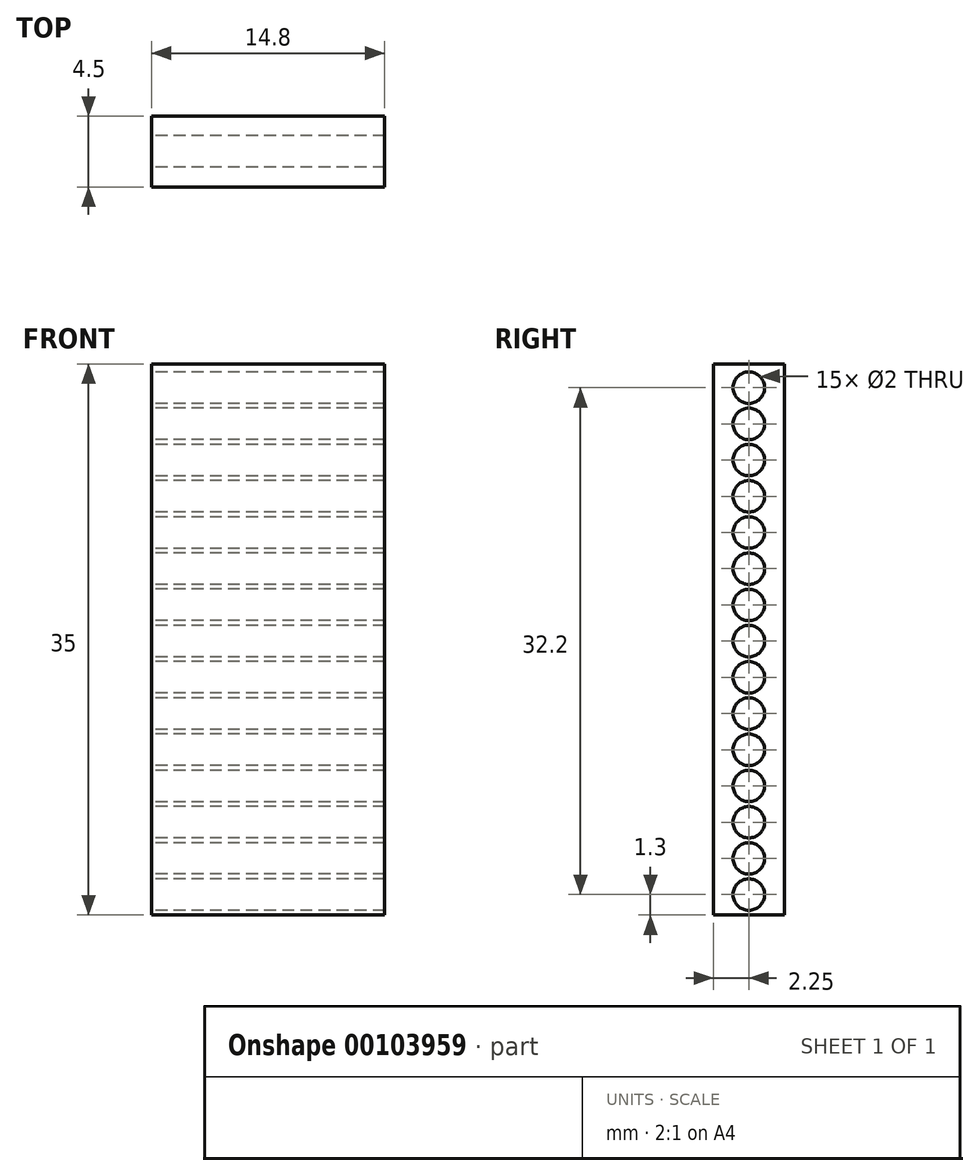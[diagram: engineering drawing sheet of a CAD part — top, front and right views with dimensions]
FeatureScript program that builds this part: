
annotation { "Feature Type Name" : "Feature", "Feature Type Description" : "" }
export const myFeature = defineFeature(function(context is Context, id is Id, definition is map)
    precondition{}
    {
        {
            var Q0;
            Q0=qCreatedBy(makeId("Front.planeOp"),FACE);
            var sketch = newSketch(context, id + "F0", { "sketchPlane" : qUnion([Q0])});
            skLineSegment(sketch, "E0.bottom", {"start": v(7.4, -17.5) * mm, "end": v(-7.4, -17.5) * mm});
            skLineSegment(sketch, "E0.top", {"start": v(7.4, 17.5) * mm, "end": v(-7.4, 17.5) * mm});
            skLineSegment(sketch, "E0.left", {"start": v(7.4, -17.5) * mm, "end": v(7.4, 17.5) * mm});
            skLineSegment(sketch, "E0.right", {"start": v(-7.4, -17.5) * mm, "end": v(-7.4, 17.5) * mm});
            skPoint(sketch, "E0.middle", {"position": v(0, 0) * mm});
            skSolve(sketch);
        }
        {
            var Q0;
            Q0 = qSketchRegion(id + "F0", true);
            extrude(context, id + "F1", {"entities" : qUnion([Q0]), "depth" : 4.5 * mm});
        }
        {
            var Q0;
            Q0=makeQuery(id+"F1.opExtrude","SWEPT_FACE",FACE,{"disambiguationData":[OSD([sQuery(id+"F0.wireOp",EDGE,"E0.right")])]});
            var sketch = newSketch(context, id + "F2", { "sketchPlane" : qUnion([Q0])});
            skCircle(sketch, "E1", {"center": v(2.25, 16) * mm, "radius": 1 * mm});
            skPoint(sketch, "E2", {"position": v(2.25, -17.5) * mm});
            skCircle(sketch, "E3.0.1.0", {"center": v(2.25, 13.7) * mm, "radius": 1 * mm});
            skCircle(sketch, "E3.0.2.0", {"center": v(2.25, 11.4) * mm, "radius": 1 * mm});
            skCircle(sketch, "E3.0.3.0", {"center": v(2.25, 9.1) * mm, "radius": 1 * mm});
            skCircle(sketch, "E3.0.4.0", {"center": v(2.25, 6.8) * mm, "radius": 1 * mm});
            skCircle(sketch, "E3.0.5.0", {"center": v(2.25, 4.5) * mm, "radius": 1 * mm});
            skCircle(sketch, "E3.0.6.0", {"center": v(2.25, 2.2) * mm, "radius": 1 * mm});
            skCircle(sketch, "E3.0.7.0", {"center": v(2.25, -0.1) * mm, "radius": 1 * mm});
            skCircle(sketch, "E3.0.8.0", {"center": v(2.25, -2.4) * mm, "radius": 1 * mm});
            skCircle(sketch, "E3.0.9.0", {"center": v(2.25, -4.7) * mm, "radius": 1 * mm});
            skCircle(sketch, "E3.0.10.0", {"center": v(2.25, -7) * mm, "radius": 1 * mm});
            skCircle(sketch, "E3.0.11.0", {"center": v(2.25, -9.3) * mm, "radius": 1 * mm});
            skCircle(sketch, "E3.0.12.0", {"center": v(2.25, -11.6) * mm, "radius": 1 * mm});
            skCircle(sketch, "E3.0.13.0", {"center": v(2.25, -13.9) * mm, "radius": 1 * mm});
            skCircle(sketch, "E3.0.14.0", {"center": v(2.25, -16.2) * mm, "radius": 1 * mm});
            skLineSegment(sketch, "E3.direction1", {"start": v(2.25, 16) * mm, "end": v(10.35, 16) * mm, "construction": true});
            skLineSegment(sketch, "E3.direction2", {"start": v(2.25, 16) * mm, "end": v(2.25, 13.7) * mm, "construction": true});
            skSolve(sketch);
        }
        {
            var Q0;
            Q0 = qSketchRegion(id + "F2", true);
            extrude(context, id + "F3", {"entities" : qUnion([Q0]), "operationType" : NewBodyOperationType.REMOVE, "endBound" : BoundingType.THROUGH_ALL, "oppositeDirection" : true, "depth" : 25 * mm});
        }
    });
